# Revit family: IS_LDV_E2637_BIM_GB
name_source: partatom
category: Plumbing Fixtures
units: mm (PartAtom-declared; Revit-internal decimal feet)

## family parameters
Cut with Voids When Loaded = No
Host = Face
Maintain Annotation Orientation = No
OmniClass Number = 23.45.05.14.14.14
OmniClass Title = Clinic Sinks
Part Type = Normal
Room Calculation Point = No
Round Connector Dimension = Use Diameter
Shared = Yes

## types (2) — shared parameters
Accessories = https://www.idealstandard.co.uk
AreaUnits = millimeters
Assembly Code = C1030200
AssetType = Fixed
BIMObjectName = IS_LDV_Bidet_E2637
Brand = Ideal Standard
Color = White
ConnectionType = Plumbing
Default Elevation = 400 mm  [stored 1.31234 ft]
DrainSize = 46 mm  [stored 0.150919 ft]
DurationUnit = year
ECA = No
EPD = https://www.idealstandard.co.uk
ExpectedLife = 30
Help = https://www.idealstandard.co.uk
IfcExportAs = IfcSanitaryType
IfcExportType = BIDET
InstallationInstructions = https://www.idealstandard.co.uk
LinearUnits = millimeters
Manufacturer = Ideal Standard
ManufacturerURL = https://www.idealstandard.co.uk
Material = Fine Fireclay
NBSDescription = Bidets
NBSReference = Pr_40_20_96_81
Name = Bidet_LDV_E2637_IdealStandard
NettWeight = 20
NominalDepth = 543 mm
NominalHeight = 315 mm
NominalLength = 543 mm
NominalWidth = 360 mm
ProductInformation = https://www.idealstandard.co.uk
Shape = Sculptured
Size = 360 x 543 x 315 mm
Space = Internal
URL = https://www.idealstandard.co.uk
Uniclass2015Code = Pr_40_20_96_81
Uniclass2015Description = Bidets
Uniclass2015Title = Bidets
Uniclass2015Version = Products v1.33
Version = 1
VolumeUnits = Litres
WRAS = No
WarrantyDescription = Manufacturers Warranty
WarrantyDurationParts = 99
WarrantyDurationUnit = year
WarrantyGuarantorParts = Ideal Standard
WaterEfficientProduct = No
zero-valued in all types: CWFU, Cost, HWFU, WFU

## per-type parameters (varying)
| type | BarCode | Description | Features | Finish | Model | ModelNumber | ModelReference |
| E263701 - LDV WH BIDET HF WHITE BXD | 5017830562467 | La Dolce Vita® wallhung bidet, hidden fixation, incl fixation set TT0299598,  1 taphole, with round overflow | La Dolce Vita® wallhung bidet, hidden fixation, incl fixation set TT0299598,  1 taphole, with round overflow, white, carton box, EU pallet | white | E263701 | E263701 | La Dolce Vita® wallhung bidet, hidden fixation, incl fixation set TT0299598,  1 taphole, with round overflow |
| E2637MA - LDV WH BIDET HF WHITE IP BXD | 5017830563884 | La Dolce Vita® wallhung bidet, hidden fixation, incl fixation set TT0299598,  1 taphole, with round overflow, white Ideal Plus | La Dolce Vita® wallhung bidet, hidden fixation, incl fixation set TT0299598,  1 taphole, with round overflow, white Ideal Plus, carton box, EU pallet | white Ideal Plus | E2637MA | E2637MA | La Dolce Vita® wallhung bidet, hidden fixation, incl fixation set TT0299598,  1 taphole, with round overflow, white Ideal Plus |

note: [stored X ft] marks values corroborated as IEEE doubles in the binary element streams (Revit-internal decimal feet)

## geometry (parser evidence)
native form markers: Sweep x2
no freeform markers — native parametric forms only
